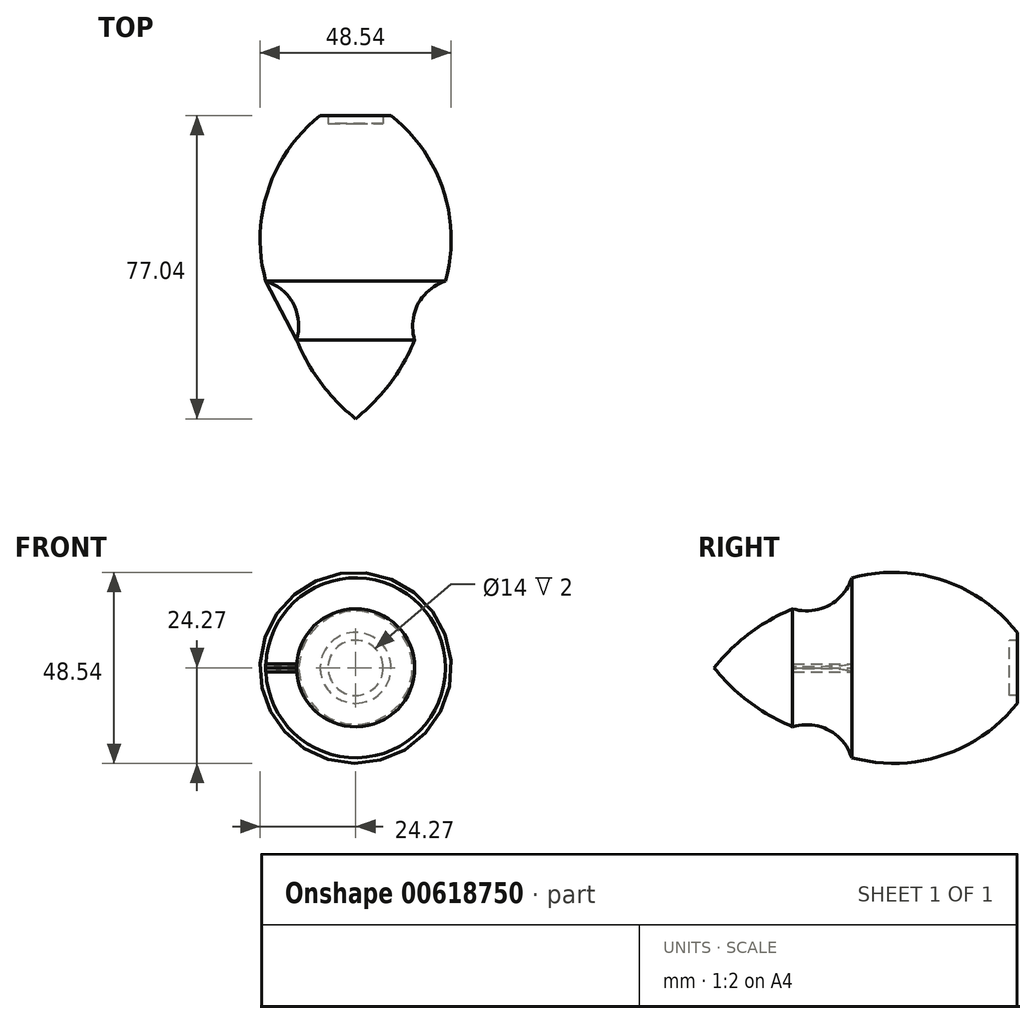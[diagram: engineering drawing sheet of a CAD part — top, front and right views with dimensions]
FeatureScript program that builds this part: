
annotation { "Feature Type Name" : "Feature", "Feature Type Description" : "" }
export const myFeature = defineFeature(function(context is Context, id is Id, definition is map)
    precondition{}
    {
        {
            var Q0;
            Q0=qCreatedBy(makeId("Top.planeOp"),FACE);
            var sketch = newSketch(context, id + "F0", { "sketchPlane" : qUnion([Q0])});
            skLineSegment(sketch, "E0", {"start": v(0, 0) * mm, "end": v(0, 77.04) * mm});
            skLineSegment(sketch, "E1", {"start": v(7, 77.04) * mm, "end": v(9, 77.04) * mm});
            skLineSegment(sketch, "E2", {"start": v(0, 20) * mm, "end": v(15, 20) * mm});
            skArc(sketch, "E3", {"start": v(22.84, 35) * mm, "mid": v(22.26, 58.1) * mm, "end": v(9, 77.04) * mm});
            skLineSegment(sketch, "E4", {"start": v(0, 35) * mm, "end": v(22.84, 35) * mm});
            skArc(sketch, "E5", {"start": v(0, 0) * mm, "mid": v(8.77, 9.05) * mm, "end": v(15, 20) * mm});
            skArc(sketch, "E6", {"start": v(22.84, 35) * mm, "mid": v(15.82, 29.12) * mm, "end": v(15, 20) * mm});
            skLineSegment(sketch, "E7", {"start": v(0, 75.04) * mm, "end": v(7, 75.04) * mm});
            skLineSegment(sketch, "E8", {"start": v(7, 75.04) * mm, "end": v(7, 77.04) * mm});
            skSolve(sketch);
        }
        {
            var Q0;
            Q0 = qSketchRegion(id + "F0", true);
            var Q1;
            Q1=sQuery(id+"F0.wireOp",EDGE,"E0");
            revolve(context, id + "F1", {"entities" : qUnion([Q0]), "axis" : qUnion([Q1]), "revolveType" : RevolveType.FULL});
        }
        {
            var Q0;
            Q0=qCreatedBy(makeId("Top.planeOp"),FACE);
            var sketch = newSketch(context, id + "F2", { "sketchPlane" : qUnion([Q0])});
            skArc(sketch, "E9", {"start": v(-15, 20) * mm, "mid": v(-15.82, 29.12) * mm, "end": v(-22.84, 35) * mm});
            skLineSegment(sketch, "E10.0", {"start": v(15, 20) * mm, "end": v(-15, 20) * mm});
            skLineSegment(sketch, "E11", {"start": v(-22.84, 35) * mm, "end": v(-15, 20) * mm});
            skSolve(sketch);
        }
        {
            var Q0;
            Q0 = qSketchRegion(id + "F2", true);
            extrude(context, id + "F3", {"entities" : qUnion([Q0]), "depth" : 25 * mm, "offsetDistance" : 25 * mm});
        }
        {
            var Q0;
            Q0=makeQuery(id+"F3.opExtrude","SWEPT_BODY",BODY,{"disambiguationData":[OSD([sQuery(id+"F2.wireOp",EDGE,"E9"),sQuery(id+"F2.wireOp",EDGE,"E11")])]});
            deleteBodies(context, id + "F4", {"entities" : qUnion([Q0])});
        }
        {
            var Q0;
            Q0=qCreatedBy(makeId("Top.planeOp"),FACE);
            var sketch = newSketch(context, id + "F5", { "sketchPlane" : qUnion([Q0])});
            skLineSegment(sketch, "E12.0", {"start": v(22.84, 35) * mm, "end": v(-22.84, 35) * mm});
            skLineSegment(sketch, "E13.0", {"start": v(15, 20) * mm, "end": v(-15, 20) * mm});
            skLineSegment(sketch, "E14", {"start": v(-22.84, 35) * mm, "end": v(-15, 20) * mm});
            skArc(sketch, "E15", {"start": v(-15, 20) * mm, "mid": v(-15.82, 29.12) * mm, "end": v(-22.84, 35) * mm});
            skSolve(sketch);
        }
        {
            var Q0;
            Q0 = qSketchRegion(id + "F5", true);
            extrude(context, id + "F6", {"entities" : qUnion([Q0]), "operationType" : NewBodyOperationType.ADD, "endBound" : BoundingType.SYMMETRIC, "depth" : 2 * mm, "offsetDistance" : 25 * mm, "hasDraft" : true, "draftAngle" : 0.5 * degree, "hasSecondDirection" : true, "secondDirectionOppositeDirection" : true, "secondDirectionDepth" : 25 * mm});
        }
    });
